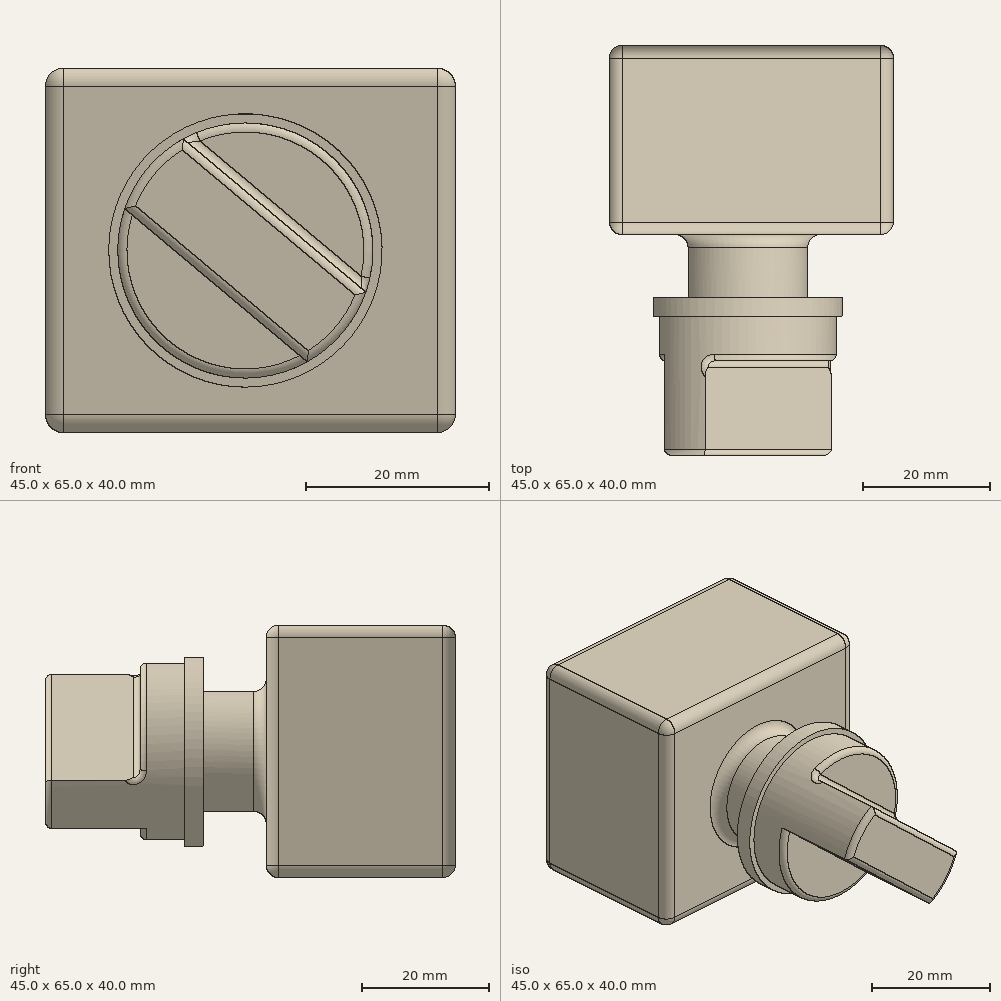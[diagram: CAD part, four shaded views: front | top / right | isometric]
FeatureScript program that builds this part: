
annotation { "Feature Type Name" : "Feature", "Feature Type Description" : "" }
export const myFeature = defineFeature(function(context is Context, id is Id, definition is map)
    precondition{}
    {
        {
            var Q0;
            Q0=qCreatedBy(makeId("Front.planeOp"),FACE);
            var sketch = newSketch(context, id + "F0", { "sketchPlane" : qUnion([Q0])});
            skCircle(sketch, "E0", {"center": v(0, 0) * mm, "radius": 15 * mm});
            skCircle(sketch, "E1", {"center": v(0, 0) * mm, "radius": 14 * mm});
            skSolve(sketch);
        }
        {
            var Q0;
            Q0=makeQuery(id+"F0.imprint","IMPRINT",FACE,{"disambiguationData":[TD([[makeQuery(id+"F0.imprint","IMPRINT",EDGE,{"derivedFrom":sQuery(id+"F0.wireOp",EDGE,"E1")}),1.0]])]});
            extrude(context, id + "F1", {"entities" : qUnion([Q0]), "depth" : 10 * mm});
        }
        {
            var Q0;
            Q0=makeQuery(id+"F0.imprint","IMPRINT",FACE,{"disambiguationData":[TD([[makeQuery(id+"F0.imprint","IMPRINT",EDGE,{"derivedFrom":sQuery(id+"F0.wireOp",EDGE,"E0")}),1.0]])]});
            extrude(context, id + "F2", {"entities" : qUnion([Q0]), "operationType" : NewBodyOperationType.ADD, "depth" : 3 * mm});
        }
        {
            var Q0;
            Q0=makeQuery(id+"F1.opExtrude","CAP_FACE",FACE,{"disambiguationData":[OSD([sQuery(id+"F0.wireOp",EDGE,"E1")])],"isStart":false});
            var sketch = newSketch(context, id + "F3", { "sketchPlane" : qUnion([Q0])});
            skLineSegment(sketch, "E2", {"start": v(-6.8, 12.24) * mm, "end": v(13.23, -4.58) * mm});
            skLineSegment(sketch, "E3", {"start": v(-13.23, 4.58) * mm, "end": v(6.8, -12.24) * mm});
            skLineSegment(sketch, "E4", {"start": v(0, 0) * mm, "end": v(0, 14) * mm, "construction": true});
            skSolve(sketch);
        }
        {
            var Q0;
            {var subQ0=sQuery(id+"F3.wireOp",EDGE,"E2");Q0=makeQuery(id+"F3.imprint","IMPRINT",FACE,{"disambiguationData":[TD([[makeQuery(id+"F3.imprint","IMPRINT",EDGE,{"derivedFrom":subQ0}),-1.0]])]});}
            extrude(context, id + "F4", {"entities" : qUnion([Q0]), "operationType" : NewBodyOperationType.ADD, "depth" : 15 * mm});
        }
        {
            var Q0;
            Q0=makeQuery(id+"F4.opExtrude","CAP_FACE",FACE,{"disambiguationData":[OSD([sQuery(id+"F0.wireOp",EDGE,"E1"),sQuery(id+"F3.wireOp",EDGE,"E2"),sQuery(id+"F3.wireOp",EDGE,"E3")])],"isStart":false});
            var Q1;
            {var subQ0=sQuery(id+"F0.wireOp",EDGE,"E1");var subQ1=sQuery(id+"F3.wireOp",EDGE,"E2");Q1=makeQuery(id+"F4.boolean.opBoolean","SPLIT",FACE,{"disambiguationData":[TD([makeQuery(id+"F4.opExtrude","SWEPT_FACE",FACE,{"disambiguationData":[OSD([subQ1])]})])],"derivedFrom":makeQuery(id+"F1.opExtrude","CAP_FACE",FACE,{"disambiguationData":[OSD([subQ0])],"isStart":false})});}
            var Q2;
            {var subQ1=sQuery(id+"F0.wireOp",EDGE,"E1");var subQ2=makeQuery(id+"F1.opExtrude","CAP_EDGE",EDGE,{"disambiguationData":[OSD([subQ1])],"isStart":false});var subQ3=sQuery(id+"F3.wireOp",EDGE,"E3");Q2=makeQuery(id+"F4.boolean.opBoolean","SPLIT",EDGE,{"disambiguationData":[TD([makeQuery(id+"F4.opExtrude","SWEPT_FACE",FACE,{"disambiguationData":[OSD([subQ3])]})])],"derivedFrom":subQ2});}
            fillet(context, id + "F5", {"entities" : qUnion([Q0, Q1, Q2]), "radius" : 1 * mm, "tangentPropagation" : true, "allowEdgeOverflow" : false});
        }
        {
            var Q0;
            Q0=makeQuery(id+"F0.imprint","IMPRINT",FACE,{"disambiguationData":[TD([[makeQuery(id+"F0.imprint","IMPRINT",EDGE,{"derivedFrom":sQuery(id+"F0.wireOp",EDGE,"E1")}),1.0]])]});
            var sketch = newSketch(context, id + "F6", { "sketchPlane" : qUnion([Q0])});
            skCircle(sketch, "E5", {"center": v(0, 0) * mm, "radius": 9.5 * mm});
            skSolve(sketch);
        }
        {
            var Q0;
            Q0=makeQuery(id+"F6.imprint","IMPRINT",FACE,{"disambiguationData":[TD([[makeQuery(id+"F6.imprint","IMPRINT",EDGE,{"derivedFrom":sQuery(id+"F6.wireOp",EDGE,"E5")}),1.0]])]});
            extrude(context, id + "F7", {"entities" : qUnion([Q0]), "operationType" : NewBodyOperationType.ADD, "oppositeDirection" : true, "depth" : 10 * mm});
        }
        {
            var Q0;
            Q0=makeQuery(id+"F7.opExtrude","CAP_FACE",FACE,{"disambiguationData":[OSD([sQuery(id+"F6.wireOp",EDGE,"E5")])],"isStart":false});
            var sketch = newSketch(context, id + "F8", { "sketchPlane" : qUnion([Q0])});
            skLineSegment(sketch, "E6.bottom", {"start": v(-23.06, 20) * mm, "end": v(21.94, 20) * mm});
            skLineSegment(sketch, "E6.top", {"start": v(-23.06, -20) * mm, "end": v(21.94, -20) * mm});
            skLineSegment(sketch, "E6.left", {"start": v(-23.06, 20) * mm, "end": v(-23.06, -20) * mm});
            skLineSegment(sketch, "E6.right", {"start": v(21.94, 20) * mm, "end": v(21.94, -20) * mm});
            skPoint(sketch, "E6.middle", {"position": v(-0.56, 0) * mm});
            skSolve(sketch);
        }
        {
            var Q0;
            Q0=makeQuery(id+"F8.imprint","IMPRINT",FACE,{"disambiguationData":[TD([[makeQuery(id+"F8.imprint","IMPRINT",EDGE,{"derivedFrom":makeQuery(id+"F7.opExtrude","CAP_EDGE",EDGE,{"disambiguationData":[OSD([sQuery(id+"F6.wireOp",EDGE,"E5")])],"isStart":false})}),-1.0]])]});
            var Q1;
            Q1=makeQuery(id+"F8.imprint","IMPRINT",FACE,{"disambiguationData":[TD([[makeQuery(id+"F8.imprint","IMPRINT",EDGE,{"derivedFrom":sQuery(id+"F8.wireOp",EDGE,"E6.bottom")}),-1.0]])]});
            extrude(context, id + "F9", {"entities" : qUnion([Q0, Q1]), "operationType" : NewBodyOperationType.ADD, "depth" : 30 * mm});
        }
        {
            var Q0;
            Q0=makeQuery(id+"F9.opExtrude","SWEPT_FACE",FACE,{"disambiguationData":[OSD([sQuery(id+"F8.wireOp",EDGE,"E6.bottom")])]});
            var Q1;
            Q1=makeQuery(id+"F9.opExtrude","SWEPT_FACE",FACE,{"disambiguationData":[OSD([sQuery(id+"F8.wireOp",EDGE,"E6.left")])]});
            var Q2;
            Q2=makeQuery(id+"F9.opExtrude","CAP_FACE",FACE,{"disambiguationData":[OSD([sQuery(id+"F8.wireOp",EDGE,"E6.bottom"),sQuery(id+"F8.wireOp",EDGE,"E6.top"),sQuery(id+"F8.wireOp",EDGE,"E6.left"),sQuery(id+"F8.wireOp",EDGE,"E6.right")])],"isStart":false});
            var Q3;
            Q3=makeQuery(id+"F9.opExtrude","SWEPT_FACE",FACE,{"disambiguationData":[OSD([sQuery(id+"F8.wireOp",EDGE,"E6.top")])]});
            var Q4;
            Q4=makeQuery(id+"F9.opExtrude","SWEPT_FACE",FACE,{"disambiguationData":[OSD([sQuery(id+"F8.wireOp",EDGE,"E6.right")])]});
            var Q5;
            Q5=makeQuery(id+"F9.opExtrude","CAP_FACE",FACE,{"disambiguationData":[OSD([sQuery(id+"F8.wireOp",EDGE,"E6.bottom"),sQuery(id+"F8.wireOp",EDGE,"E6.top"),sQuery(id+"F8.wireOp",EDGE,"E6.left"),sQuery(id+"F8.wireOp",EDGE,"E6.right")])],"isStart":true});
            fillet(context, id + "F10", {"entities" : qUnion([Q0, Q1, Q2, Q3, Q4, Q5]), "radius" : 2 * mm, "tangentPropagation" : true, "allowEdgeOverflow" : false});
        }
    });
